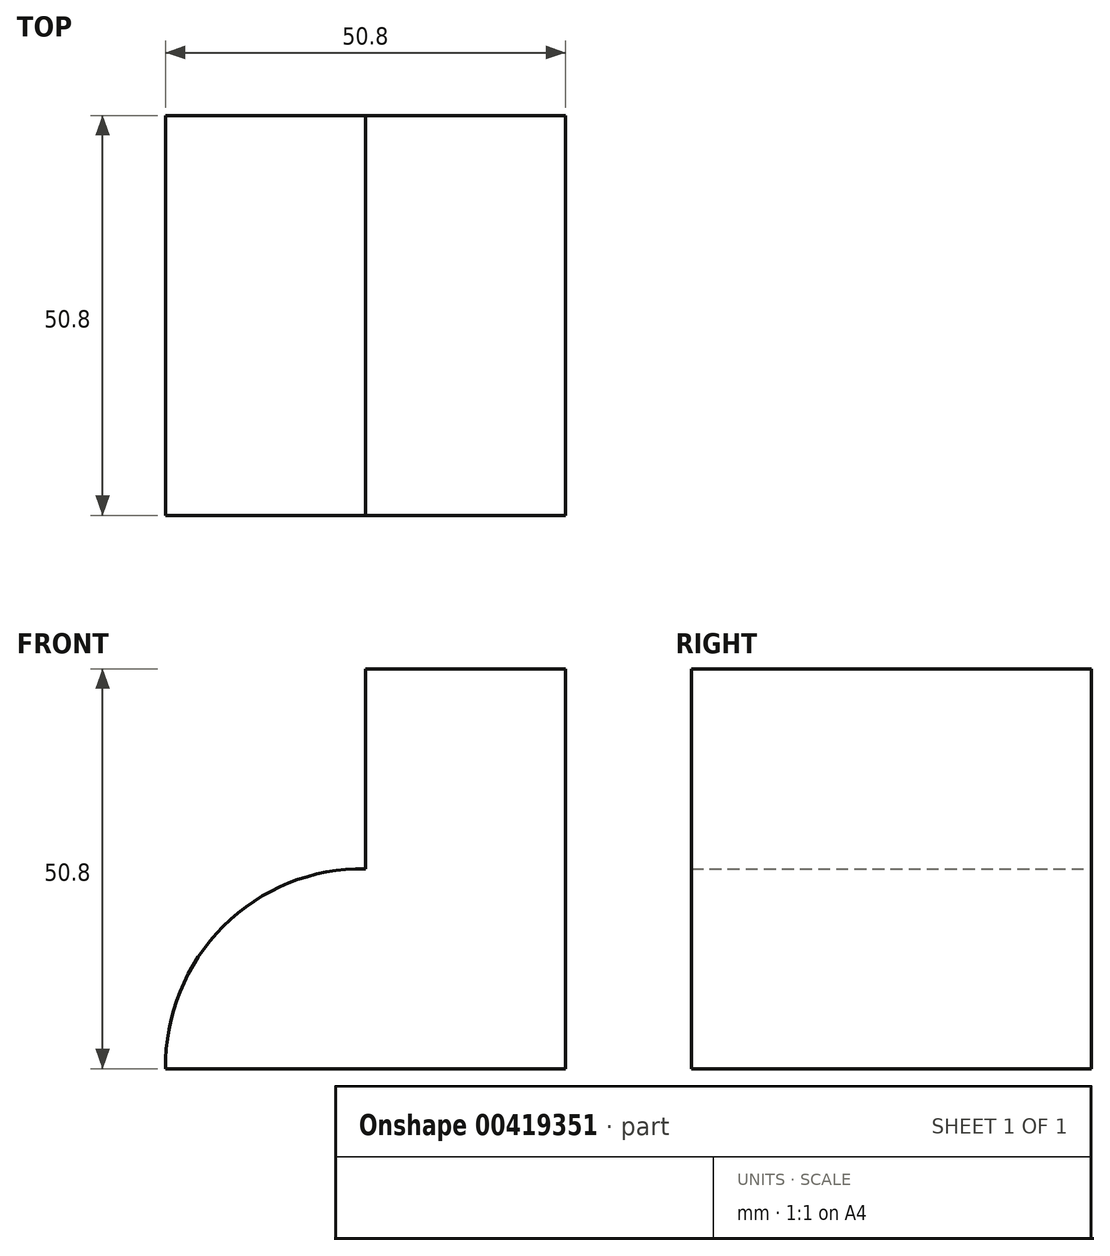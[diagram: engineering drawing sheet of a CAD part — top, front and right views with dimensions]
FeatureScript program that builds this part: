
annotation { "Feature Type Name" : "Feature", "Feature Type Description" : "" }
export const myFeature = defineFeature(function(context is Context, id is Id, definition is map)
    precondition{}
    {
        {
            var Q0;
            Q0=qCreatedBy(makeId("Front.planeOp"),FACE);
            var sketch = newSketch(context, id + "F0", { "sketchPlane" : qUnion([Q0])});
            skLineSegment(sketch, "E0", {"start": v(-27.12, -28.45) * mm, "end": v(23.68, -28.45) * mm});
            skLineSegment(sketch, "E1", {"start": v(23.68, -28.45) * mm, "end": v(23.68, 22.35) * mm});
            skLineSegment(sketch, "E2", {"start": v(23.68, 22.35) * mm, "end": v(-1.72, 22.35) * mm});
            skLineSegment(sketch, "E3", {"start": v(-1.72, 22.35) * mm, "end": v(-1.72, -3.05) * mm});
            skArc(sketch, "E4", {"start": v(-1.72, -3.05) * mm, "mid": v(-19.8, -10.38) * mm, "end": v(-27.12, -28.45) * mm});
            skSolve(sketch);
        }
        {
            var Q0;
            Q0 = qSketchRegion(id + "F0", true);
            extrude(context, id + "F1", {"entities" : qUnion([Q0]), "depth" : 50.8 * mm});
        }
    });
